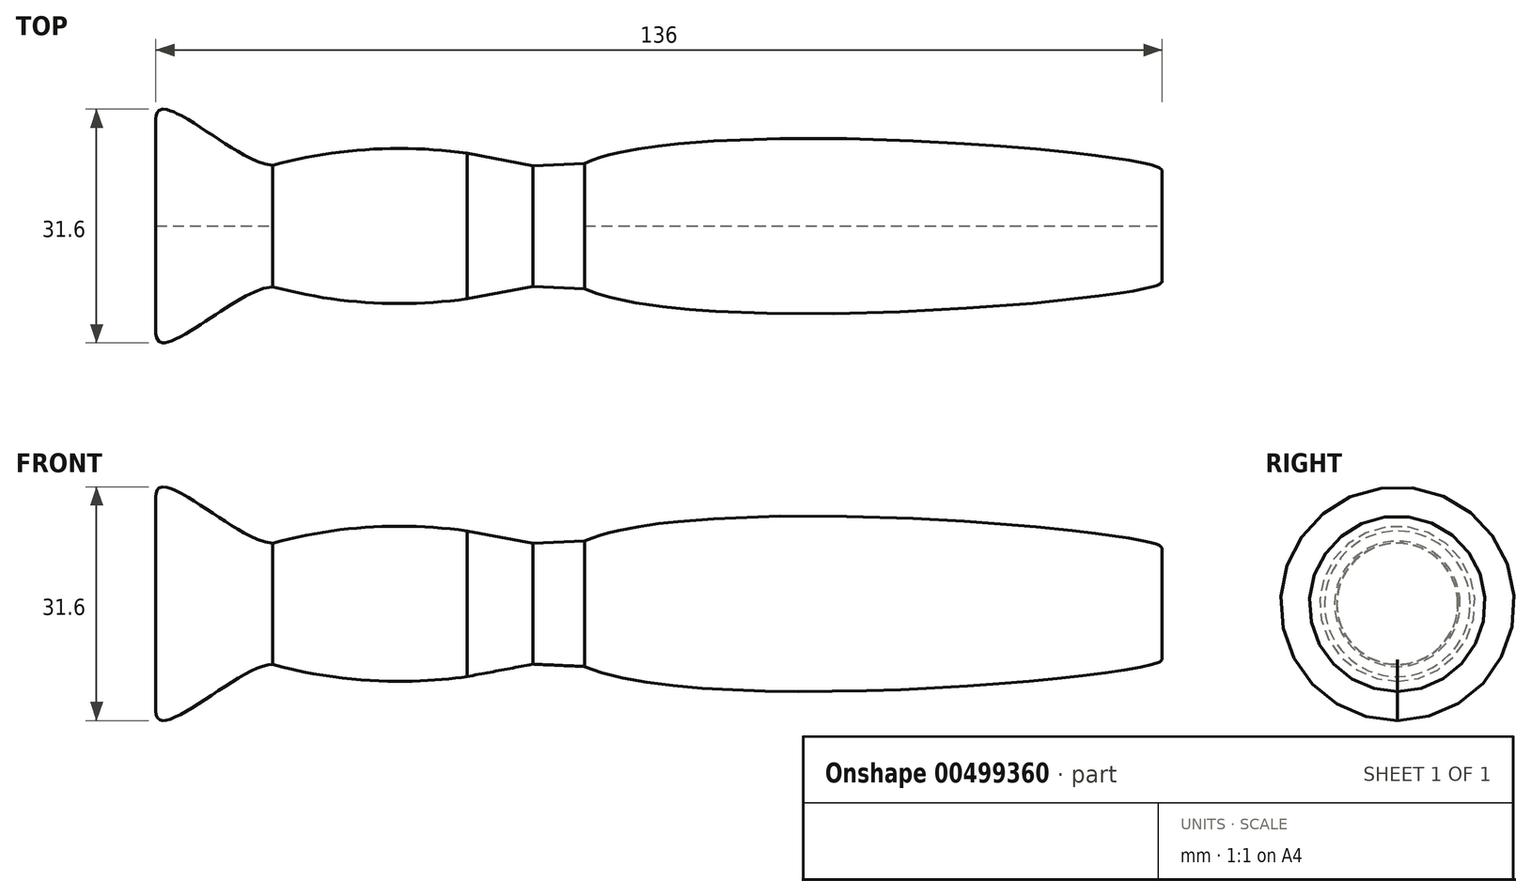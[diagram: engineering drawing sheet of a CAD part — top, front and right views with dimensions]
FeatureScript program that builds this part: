
annotation { "Feature Type Name" : "Feature", "Feature Type Description" : "" }
export const myFeature = defineFeature(function(context is Context, id is Id, definition is map)
    precondition{}
    {
        {
            var Q0;
            Q0=qCreatedBy(makeId("Front.planeOp"),FACE);
            var sketch = newSketch(context, id + "F0", { "sketchPlane" : qUnion([Q0])});
            skLineSegment(sketch, "E0", {"start": v(136, 0) * mm, "end": v(0, 0) * mm});
            skLineSegment(sketch, "E1", {"start": v(0, 0) * mm, "end": v(0, 14.5) * mm});
            skLineSegment(sketch, "E2", {"start": v(42.1, 9.84) * mm, "end": v(50.94, 8.16) * mm});
            skLineSegment(sketch, "E3", {"start": v(50.94, 8.16) * mm, "end": v(57.93, 8.48) * mm});
            skLineSegment(sketch, "E4", {"start": v(136, 0) * mm, "end": v(136, 7.57) * mm});
            skFitSpline(sketch, "E5", {"points": [v(57.93, 8.48) * mm, v(136, 7.57) * mm], "startDerivative": vector(48.26, 20.93) * mm, "endDerivative": vector(0, -6.83) * mm});
            skFitSpline(sketch, "E6", {"points": [v(0, 14.5) * mm, v(15.8, 8.22) * mm], "startDerivative": vector(0, 15.14) * mm, "endDerivative": vector(13.8, 0) * mm});
            skFitSpline(sketch, "E7", {"points": [v(15.8, 8.22) * mm, v(42.1, 9.84) * mm], "startDerivative": vector(32.17, 8.81) * mm, "endDerivative": vector(17.8, -2.56) * mm});
            skSolve(sketch);
        }
        {
            var Q0;
            Q0=makeQuery(id+"F0.imprint","IMPRINT",FACE,{"disambiguationData":[TD([[makeQuery(id+"F0.imprint","IMPRINT",EDGE,{"derivedFrom":sQuery(id+"F0.wireOp",EDGE,"E0")}),-1.0]])]});
            var Q1;
            Q1=sQuery(id+"F0.wireOp",EDGE,"E0");
            revolve(context, id + "F1", {"entities" : qUnion([Q0]), "axis" : qUnion([Q1]), "revolveType" : RevolveType.SYMMETRIC, "angle" : 360 * degree});
        }
    });
